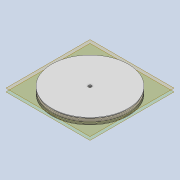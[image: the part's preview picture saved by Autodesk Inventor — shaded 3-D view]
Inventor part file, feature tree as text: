
AUTODESK INVENTOR PART (.ipt)
format: ipt  version: 2020 (Build 240168000, 168)  size: 162,816 bytes
history: native  units: mm
features: sketch x3, extrude x2, plane x2, revolve x1, fillet x1
ambient origin geometry x8: Origin, YZ Plane, XZ Plane, XY Plane, X Axis, Y Axis, Z Axis, Center Point
bodies: Solid1 (feature_tree)
feature tree (9):
  extrude  "Extrusion1"  Depth=6.0mm TaperAngle=0.0deg
  plane  "Work Plane1"
  plane  "Work Plane2"
  extrude  "Extrusion2"  [1 undecoded]
  revolve  "Revolution1"  [1 undecoded]
  fillet  "Fillet1"  Radius=1.6mm
  sketch  "Sketch1"  dims[d0=70.0mm d1=6.0mm d2=0.0mm]
  sketch  "Sketch2"  dims[d3=-1.5mm d4=-1.5mm]
  sketch  "Sketch3"  dims[d5=3.0mm d6=6.0mm d7=0.0mm d8=1.6mm d9=0.5mm d10=2.0mm d11=2.0mm d12=1.6mm d13=0.5mm d14=2.0mm d15=2.0mm d16=10.0mm d17=90.0deg d18=0.5mm]
note: 2 required parameter values undecoded (feature->parameter linkage not recoverable at this tier; creation-order binding heuristic only, values carry confidence <= 0.55)